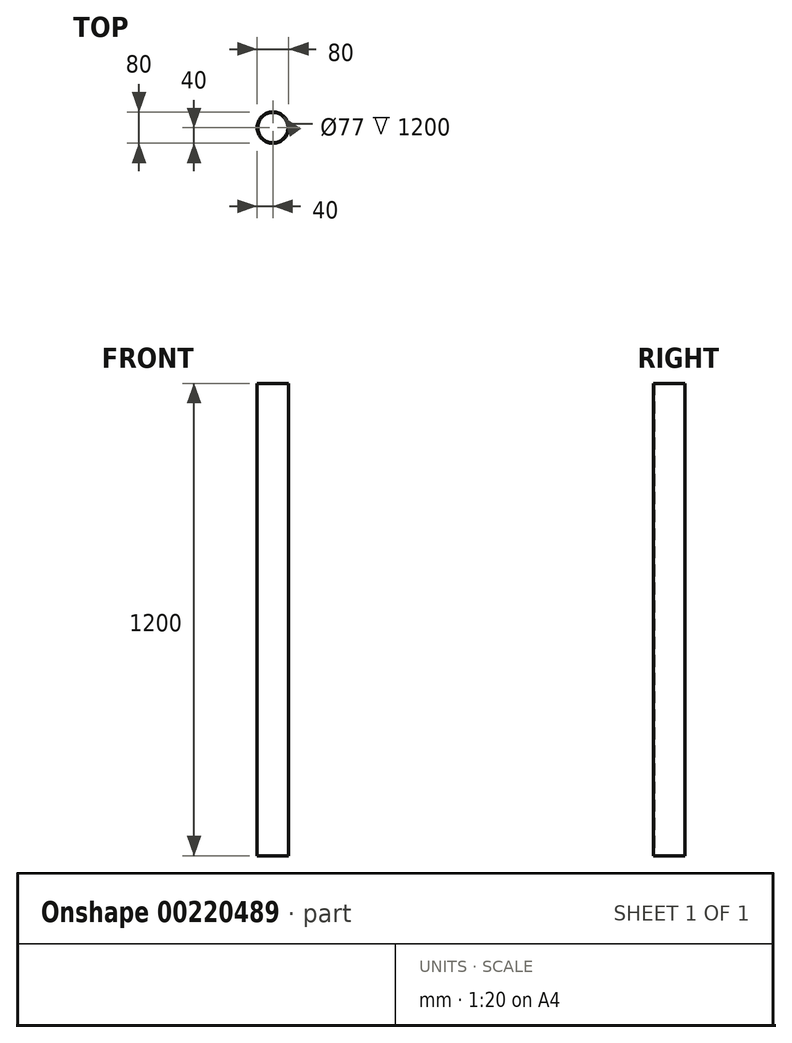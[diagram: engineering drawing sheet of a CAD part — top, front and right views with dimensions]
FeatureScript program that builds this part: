
annotation { "Feature Type Name" : "Feature", "Feature Type Description" : "" }
export const myFeature = defineFeature(function(context is Context, id is Id, definition is map)
    precondition{}
    {
        {
            var Q0;
            Q0=qCreatedBy(makeId("Top.planeOp"),FACE);
            var sketch = newSketch(context, id + "F0", { "sketchPlane" : qUnion([Q0])});
            skCircle(sketch, "E0", {"center": v(0, 0) * mm, "radius": 40 * mm});
            skCircle(sketch, "E1", {"center": v(0, 0) * mm, "radius": 38.5 * mm});
            skSolve(sketch);
        }
        {
            var Q0;
            Q0=makeQuery(id+"F0.imprint","IMPRINT",FACE,{"disambiguationData":[TD([[makeQuery(id+"F0.imprint","IMPRINT",EDGE,{"derivedFrom":sQuery(id+"F0.wireOp",EDGE,"E0")}),1.0]])]});
            extrude(context, id + "F1", {"entities" : qUnion([Q0]), "depth" : 1200 * mm});
        }
    });
